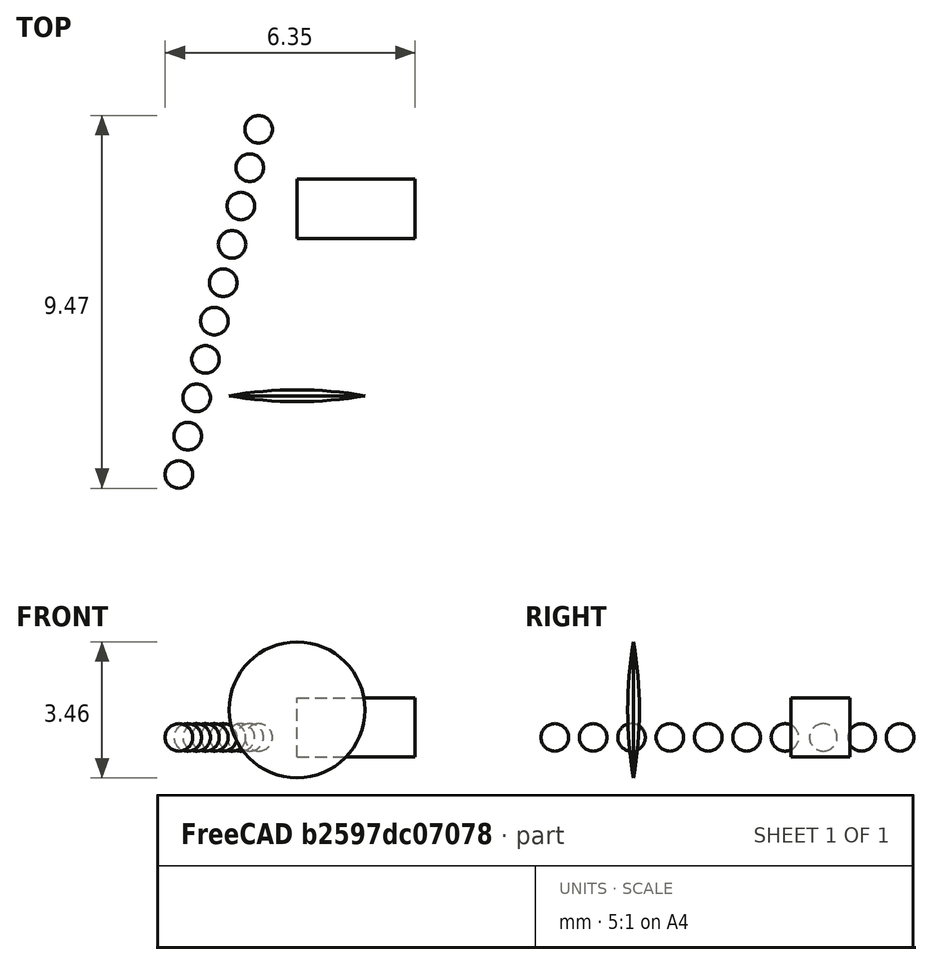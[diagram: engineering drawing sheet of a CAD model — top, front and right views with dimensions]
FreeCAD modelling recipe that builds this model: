
FCSTD DOCUMENT  (FreeCAD 0.18.3R)
Label: Lens
License: All rights reserved
LicenseURL: http://en.wikipedia.org/wiki/All_rights_reserved
objects: Part::Sphere×3, Part::MultiCommon×1, Part::Box×1, Part::FeaturePython×1
note: 6 computed .brp shape members not serialized (recipe doc carries the construction recipe); baked Part::Feature solids carry a one-line shape summary decoded from their .brp

FEATURE [Part::Sphere] Sphere
  Angle1 = -90
  Angle2 = 90
  Angle3 = 360
  AttacherType = Attacher::AttachEngine3D
  Placement = pos=(0,9.85,0) rot=(0,0,1;0rad)
  Radius = 10
FEATURE [Part::Sphere] Sphere001
  Angle1 = -90
  Angle2 = 90
  Angle3 = 360
  AttacherType = Attacher::AttachEngine3D
  Placement = pos=(0,-9.85,0) rot=(0,0,1;0rad)
  Radius = 10
FEATURE [Part::MultiCommon] Common  label="Lens"
  Placement = pos=(0,0,1.2) rot=(0,0,1;0rad)
  Shapes = -> [Sphere,Sphere001]
FEATURE [Part::Box] Box  label="Cube"
  AttacherType = Attacher::AttachEngine3D
  Height = 1.5
  Length = 3
  Placement = pos=(0,4,0) rot=(0,0,1;0rad)
  Width = 1.5
FEATURE [Part::Sphere] Sphere002
  Angle1 = -90
  Angle2 = 90
  Angle3 = 360
  AttacherType = Attacher::AttachEngine3D
  Radius = 0.35
FEATURE [Part::FeaturePython] Array  label="Spheres"  # Draft array (typed FeaturePython)
  Angle = 360
  ArrayType = 0
  Axis = (0,0,1)
  Base = -> Sphere002
  Center = (0,0,0)
  Fuse = false
  IntervalAxis = (0,0,0)
  IntervalX = (1,0,0)
  IntervalY = (0,1,0)
  IntervalZ = (0,0,1)
  NumberPolar = 10
  NumberX = 1
  NumberY = 10
  NumberZ = 1
  Placement = pos=(-3,-2,0.5) rot=(0,0,1;-0.226893rad)
